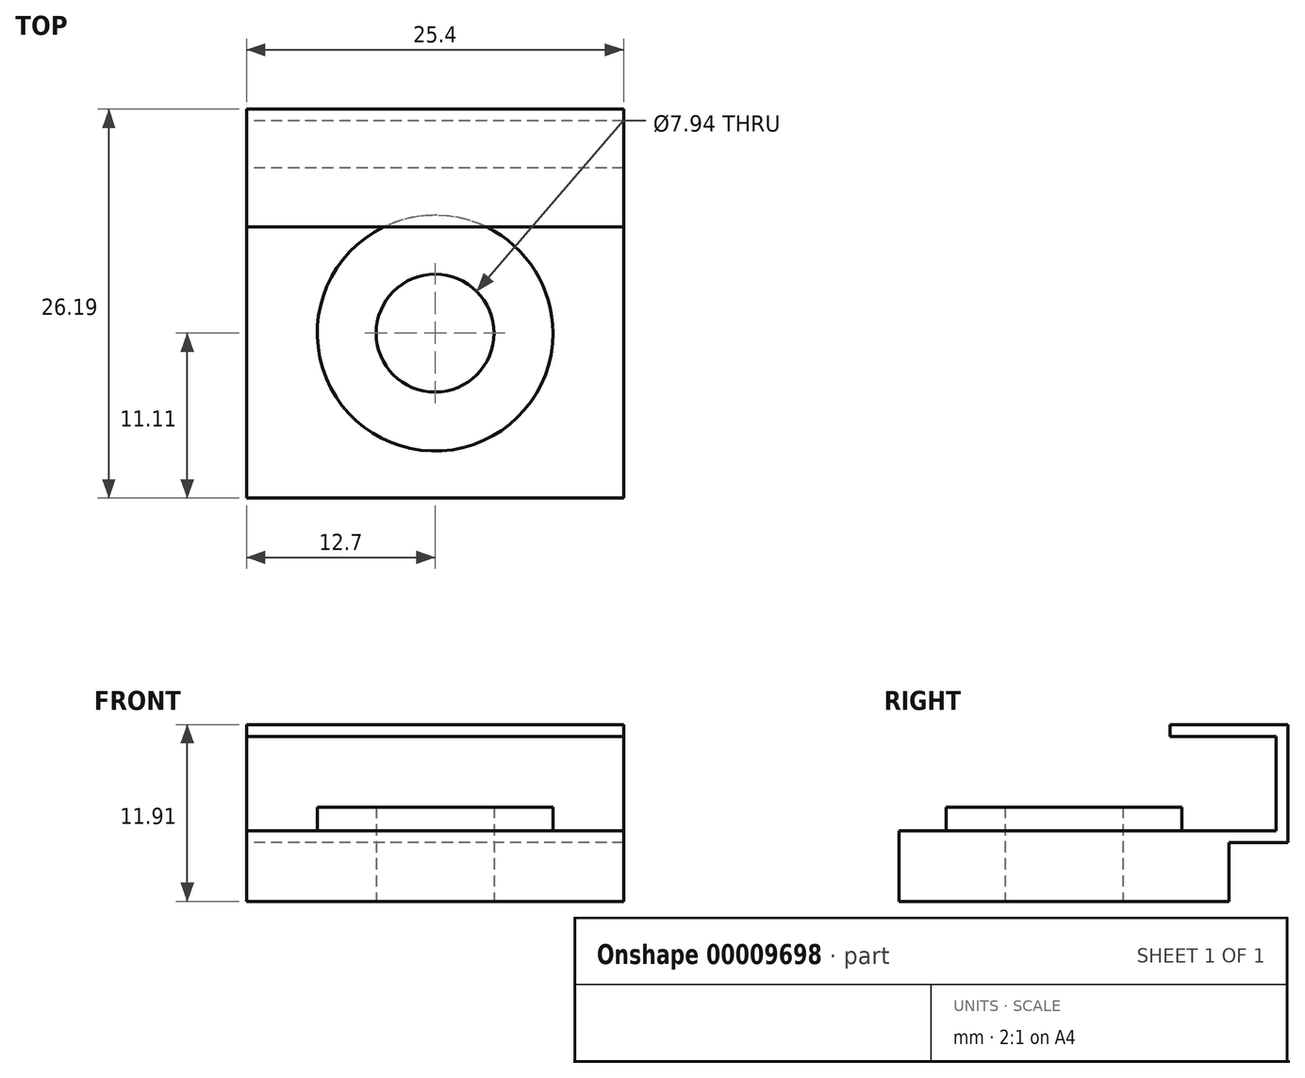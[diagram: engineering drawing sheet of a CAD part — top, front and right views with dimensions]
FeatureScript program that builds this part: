
annotation { "Feature Type Name" : "Feature", "Feature Type Description" : "" }
export const myFeature = defineFeature(function(context is Context, id is Id, definition is map)
    precondition{}
    {
        {
            var Q0;
            Q0=qCreatedBy(makeId("Top.planeOp"),FACE);
            var sketch = newSketch(context, id + "F0", { "sketchPlane" : qUnion([Q0])});
            skLineSegment(sketch, "E0.rect.bottom", {"start": v(12.7, 11.11) * mm, "end": v(-12.7, 11.11) * mm});
            skLineSegment(sketch, "E0.rect.top", {"start": v(12.7, -11.11) * mm, "end": v(-12.7, -11.11) * mm});
            skLineSegment(sketch, "E0.rect.left", {"start": v(12.7, 11.11) * mm, "end": v(12.7, -11.11) * mm});
            skLineSegment(sketch, "E0.rect.right", {"start": v(-12.7, 11.11) * mm, "end": v(-12.7, -11.11) * mm});
            skPoint(sketch, "E0.rect.middle", {"position": v(0, 0) * mm});
            skCircle(sketch, "E1", {"center": v(0, 0) * mm, "radius": 3.97 * mm});
            skSolve(sketch);
        }
        {
            var Q0;
            Q0=makeQuery(id+"F0.imprint","IMPRINT",FACE,{"disambiguationData":[TD([[makeQuery(id+"F0.imprint","IMPRINT",EDGE,{"derivedFrom":sQuery(id+"F0.wireOp",EDGE,"E0.rect.bottom")}),1.0]])]});
            extrude(context, id + "F1", {"entities" : qUnion([Q0]), "depth" : 4.76 * mm});
        }
        {
            var Q0;
            Q0=makeQuery(id+"F1.opExtrude","CAP_FACE",FACE,{"disambiguationData":[OSD([sQuery(id+"F0.wireOp",EDGE,"E0.rect.bottom"),sQuery(id+"F0.wireOp",EDGE,"E0.rect.top"),sQuery(id+"F0.wireOp",EDGE,"E0.rect.left"),sQuery(id+"F0.wireOp",EDGE,"E0.rect.right"),sQuery(id+"F0.wireOp",EDGE,"E1")])],"isStart":false});
            var sketch = newSketch(context, id + "F2", { "sketchPlane" : qUnion([Q0])});
            skCircle(sketch, "E2", {"center": v(0, 0) * mm, "radius": 7.94 * mm});
            skSolve(sketch);
        }
        {
            var Q0;
            Q0=makeQuery(id+"F2.imprint","IMPRINT",FACE,{"disambiguationData":[TD([[makeQuery(id+"F2.imprint","IMPRINT",EDGE,{"derivedFrom":sQuery(id+"F2.wireOp",EDGE,"E2")}),1.0]])]});
            extrude(context, id + "F3", {"entities" : qUnion([Q0]), "operationType" : NewBodyOperationType.ADD, "depth" : 1.59 * mm});
        }
        {
            var Q0;
            Q0=makeQuery(id+"F1.opExtrude","SWEPT_FACE",FACE,{"disambiguationData":[OSD([sQuery(id+"F0.wireOp",EDGE,"E0.rect.right")])]});
            var sketch = newSketch(context, id + "F4", { "sketchPlane" : qUnion([Q0])});
            skLineSegment(sketch, "E3", {"start": v(-11.11, 4.76) * mm, "end": v(-14.29, 4.76) * mm});
            skLineSegment(sketch, "E4", {"start": v(-14.29, 4.76) * mm, "end": v(-14.29, 11.11) * mm});
            skLineSegment(sketch, "E5", {"start": v(-14.29, 11.11) * mm, "end": v(-7.14, 11.11) * mm});
            skLineSegment(sketch, "E6", {"start": v(-7.14, 11.11) * mm, "end": v(-7.14, 11.9) * mm});
            skLineSegment(sketch, "E7", {"start": v(-7.14, 11.9) * mm, "end": v(-15.08, 11.9) * mm});
            skLineSegment(sketch, "E8", {"start": v(-15.08, 11.9) * mm, "end": v(-15.08, 3.97) * mm});
            skLineSegment(sketch, "E9", {"start": v(-15.08, 3.97) * mm, "end": v(-11.11, 3.97) * mm});
            skLineSegment(sketch, "E10", {"start": v(-11.11, 3.97) * mm, "end": v(-11.11, 4.76) * mm});
            skLineSegment(sketch, "E11", {"start": v(-15.08, 7.94) * mm, "end": v(-14.29, 7.94) * mm, "construction": true});
            skSolve(sketch);
        }
        {
            var Q0;
            Q0=qSketchRegion(id+"F4",true);
            var Q1;
            Q1=makeQuery(id+"F1.opExtrude","SWEPT_FACE",FACE,{"disambiguationData":[OSD([sQuery(id+"F0.wireOp",EDGE,"E0.rect.left")])]});
            extrude(context, id + "F5", {"entities" : qUnion([Q0]), "operationType" : NewBodyOperationType.ADD, "endBound" : BoundingType.UP_TO_SURFACE, "oppositeDirection" : true, "endBoundEntityFace" : qUnion([Q1]), "depth" : 25.4 * mm});
        }
    });
